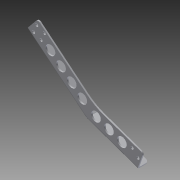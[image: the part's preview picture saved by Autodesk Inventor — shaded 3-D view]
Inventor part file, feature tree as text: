
AUTODESK INVENTOR PART (.ipt)
format: ipt  version: 2014 SP1 (Build 180222100, 222)  size: 183,296 bytes
history: native  units: in
note: dims shown in document units (in); Inventor stores cm internally (conversion verified against a paired STEP export)
features: other x3, sketch x1
ambient origin geometry x8: Origin, YZ Plane, XZ Plane, XY Plane, X Axis, Y Axis, Z Axis, Center Point
bodies: Solid1 (feature_tree)
feature tree (4):
  other  "V5 Shooter Frame Channel P5.ipt"
  other  "Solid1::V5 Shooter Frame Channel P5.ipt"
  sketch  "Sketch1"  dims[d0=0.3937in]
  other  "TaggingFeature1"
